# Revit family: AB14G
name_source: partatom
category: Generic Models
revit_build: Autodesk Revit LT 2017 (Build: 20170118_1100(x64)
units: mm (PartAtom-declared; Revit-internal decimal feet)

## family parameters
Always vertical = No
Can host rebar = No
Cut with Voids When Loaded = No
Part Type = Normal
Room Calculation Point = No
Round Connector Dimension = Use Diameter
Shared = No
Work Plane-Based = Yes

## types (1)
- NBS Standard Parameters
    BIMObjectName = metpro_metprolibrary_surfaceboxes_adaptablebox_plainsided
    Default Elevation = 1219 mm
    Description = AB14G - 150x150x75mm (6x6x3 inch ) Adaptable Box - Plain
    DurationUnit = year
    Finish = Pre Galvanised Sheet Steel
    Keynote = Complaint to LU standard 1-085
    ManufacturerName = Metpro Ltd
    ManufacturerURL = ww.metpro.co.uk
    Material = Galvanised Steel Sheet
    ModelReference = AB14G
    NBSDescription = Surface Boxes
    NBSReference = 45-35-00/340
    NominalHeight = 75 mm
    NominalLength = 150 mm
    NominalWidth = 150 mm
    ProductInformation = www.metpro.co.uk/pdf/ab14g.pdf
    Shape = Square
    Size = 150x150x75mm (6x6x3 inches)
    Uniclass2 = Pr_65_52_01_86
    Version = 1
    WarrantyDurationUnit = 1 year
    Weight = 0.7685Kg

## geometry (parser evidence)
native form markers: Sweep x2
no freeform markers — native parametric forms only
